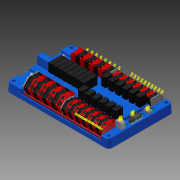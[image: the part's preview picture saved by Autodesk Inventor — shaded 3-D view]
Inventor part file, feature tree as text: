
AUTODESK INVENTOR PART (.ipt)
format: ipt  version: 2011 (Build 150239000, 239)  size: 17,145,856 bytes
history: native  units: in
note: dims shown in document units (in); Inventor stores cm internally (conversion verified against a paired STEP export)
features: other x181, sketch x22, plane x21, pattern_linear x3
ambient origin geometry x8: Origin, YZ Plane, XZ Plane, XY Plane, X Axis, Y Axis, Z Axis, Center Point
bodies: Solid1 (feature_tree)
feature tree (227):
  other  "PD Rev3 Assembly.iam"
  other  "PD Rev3 Bottom.ipt:1"
  other  "CTF040V8.iam:1::CTF040V8_1.ipt:1"
  other  "CTF040V8.iam:1::CTF040V8_2.ipt:1"
  other  "CTF040V8.iam:1::CTF040V8_3.ipt:1"
  other  "PD Rev3 PCB.iam:1::PD Rev3 Board.ipt:1"
  other  "PD Rev3 PCB.iam:1::Wago 745-831 (32A) Block.iam:1::Wago 745-831 (32A):1"
  other  "PD Rev3 PCB.iam:1::Wago 745-831 (32A) Block.iam:1::Wago 745-831 (32A):2"
  other  "PD Rev3 PCB.iam:1::Wago 745-831 (32A) Block.iam:1::Wago 745-831 (32A):3"
  other  "PD Rev3 PCB.iam:1::Wago 745-831 (32A) Block.iam:1::Wago 745-831 (32A):4"
  other  "PD Rev3 PCB.iam:1::Wago 745-831 (32A) Block.iam:1::Wago 745-831 (32A):5"
  other  "PD Rev3 PCB.iam:1::Wago 745-831 (32A) Block.iam:1::Wago 745-831 (32A):6"
  other  "PD Rev3 PCB.iam:1::Wago 745-831 (32A) Block.iam:1::Wago 745-831 (32A):7"
  other  "PD Rev3 PCB.iam:1::Wago 745-831 (32A) Block.iam:1::Wago 745-831 (32A):8"
  other  "PD Rev3 PCB.iam:1::Wago 745-831 (32A) Block.iam:1::Wago 745-831 (32A):9"
  other  "PD Rev3 PCB.iam:1::Wago 745-831 (32A) Block.iam:1::Wago 745-831 (32A):10"
  other  "PD Rev3 PCB.iam:1::Wago 745-831 (32A) Block.iam:1::Wago 745-831 (32A):11"
  other  "PD Rev3 PCB.iam:1::Wago 745-831 (32A) Block.iam:1::Wago 745-831 (32A):12"
  other  "PD Rev3 PCB.iam:1::Wago 745-831 (32A) Block.iam:1::745-300:1"
  other  "PD Rev3 PCB.iam:1::Wago 745-831 (32A) Block.iam:2::Wago 745-831 (32A):1"
  other  "PD Rev3 PCB.iam:1::Wago 745-831 (32A) Block.iam:2::Wago 745-831 (32A):2"
  other  "PD Rev3 PCB.iam:1::Wago 745-831 (32A) Block.iam:2::Wago 745-831 (32A):3"
  other  "PD Rev3 PCB.iam:1::Wago 745-831 (32A) Block.iam:2::Wago 745-831 (32A):4"
  other  "PD Rev3 PCB.iam:1::Wago 745-831 (32A) Block.iam:2::Wago 745-831 (32A):5"
  other  "PD Rev3 PCB.iam:1::Wago 745-831 (32A) Block.iam:2::Wago 745-831 (32A):6"
  other  "PD Rev3 PCB.iam:1::Wago 745-831 (32A) Block.iam:2::Wago 745-831 (32A):7"
  other  "PD Rev3 PCB.iam:1::Wago 745-831 (32A) Block.iam:2::Wago 745-831 (32A):8"
  other  "PD Rev3 PCB.iam:1::Wago 745-831 (32A) Block.iam:2::Wago 745-831 (32A):9"
  other  "PD Rev3 PCB.iam:1::Wago 745-831 (32A) Block.iam:2::Wago 745-831 (32A):10"
  other  "PD Rev3 PCB.iam:1::Wago 745-831 (32A) Block.iam:2::Wago 745-831 (32A):11"
  other  "PD Rev3 PCB.iam:1::Wago 745-831 (32A) Block.iam:2::Wago 745-831 (32A):12"
  other  "PD Rev3 PCB.iam:1::Wago 745-831 (32A) Block.iam:2::745-300:1"
  other  "PD Rev3 PCB.iam:1::Wago 745-851 (76A) Block.iam:1::Wago 745-851 (76A):2"
  other  "PD Rev3 PCB.iam:1::Wago 745-851 (76A) Block.iam:1::Wago 745-851 (76A):1"
  other  "PD Rev3 PCB.iam:1::Wago 745-851 (76A) Block.iam:1::Wago 745-851 (76A):3"
  other  "PD Rev3 PCB.iam:1::Wago 745-851 (76A) Block.iam:1::Wago 745-851 (76A):4"
  other  "PD Rev3 PCB.iam:1::Wago 745-851 (76A) Block.iam:1::Wago 745-851 (76A):5"
  other  "PD Rev3 PCB.iam:1::Wago 745-851 (76A) Block.iam:1::Wago 745-851 (76A):6"
  other  "PD Rev3 PCB.iam:1::Wago 745-851 (76A) Block.iam:1::Wago 745-851 (76A):7"
  other  "PD Rev3 PCB.iam:1::Wago 745-851 (76A) Block.iam:1::Wago 745-851 (76A):8"
  other  "PD Rev3 PCB.iam:1::Wago 745-851 (76A) Block.iam:1::745-500:1"
  other  "PD Rev3 PCB.iam:1::Wago 745-851 (76A) Block.iam:2::Wago 745-851 (76A):2"
  other  "PD Rev3 PCB.iam:1::Wago 745-851 (76A) Block.iam:2::Wago 745-851 (76A):1"
  other  "PD Rev3 PCB.iam:1::Wago 745-851 (76A) Block.iam:2::Wago 745-851 (76A):3"
  other  "PD Rev3 PCB.iam:1::Wago 745-851 (76A) Block.iam:2::Wago 745-851 (76A):4"
  other  "PD Rev3 PCB.iam:1::Wago 745-851 (76A) Block.iam:2::Wago 745-851 (76A):5"
  other  "PD Rev3 PCB.iam:1::Wago 745-851 (76A) Block.iam:2::Wago 745-851 (76A):6"
  other  "PD Rev3 PCB.iam:1::Wago 745-851 (76A) Block.iam:2::Wago 745-851 (76A):7"
  other  "PD Rev3 PCB.iam:1::Wago 745-851 (76A) Block.iam:2::Wago 745-851 (76A):8"
  other  "PD Rev3 PCB.iam:1::Wago 745-851 (76A) Block.iam:2::745-500:1"
  other  "PD Rev3 PCB.iam:1::LED.ipt:1"
  other  "PD Rev3 PCB.iam:1::LED.ipt:2"
  other  "PD Rev3 PCB.iam:1::734-132:1"
  other  "PD Rev3 PCB.iam:1::LED.ipt:3"
  other  "PD Rev3 PCB.iam:1::Wurth Lug.ipt:1"
  other  "PD Rev3 PCB.iam:1::Wurth Lug.ipt:2"
  other  "PD Rev3 PCB.iam:1::Big CB in Holder.ipt:1"
  other  "PD Rev3 PCB.iam:1::Big CB in Holder.ipt:2"
  other  "PD Rev3 PCB.iam:1::Big CB in Holder.ipt:3"
  other  "PD Rev3 PCB.iam:1::Big CB in Holder.ipt:4"
  other  "PD Rev3 PCB.iam:1::Big CB in Holder.ipt:5"
  other  "PD Rev3 PCB.iam:1::Big CB in Holder.ipt:6"
  other  "PD Rev3 PCB.iam:1::Big CB in Holder.ipt:7"
  other  "PD Rev3 PCB.iam:1::Big CB in Holder.ipt:8"
  other  "PD Rev3 PCB.iam:1::Medium CB in Holder.ipt:2"
  other  "PD Rev3 PCB.iam:1::Medium CB in Holder.ipt:1"
  other  "PD Rev3 PCB.iam:1::Medium CB in Holder.ipt:3"
  other  "PD Rev3 PCB.iam:1::Medium CB in Holder.ipt:4"
  other  "PD Rev3 PCB.iam:1::Medium CB in Holder.ipt:5"
  other  "PD Rev3 PCB.iam:1::Medium CB in Holder.ipt:6"
  other  "PD Rev3 PCB.iam:1::Medium CB in Holder.ipt:7"
  other  "PD Rev3 PCB.iam:1::Medium CB in Holder.ipt:8"
  other  "PD Rev3 PCB.iam:1::Medium CB in Holder.ipt:9"
  other  "PD Rev3 PCB.iam:1::Medium CB in Holder.ipt:10"
  other  "PD Rev3 PCB.iam:1::Medium CB in Holder.ipt:11"
  other  "PD Rev3 PCB.iam:1::Medium CB in Holder.ipt:12"
  other  "PD Rev3 PCB.iam:1::739-302:1"
  other  "PD Rev3 PCB.iam:1::CTM040V8.ipt:1"
  other  "PD Rev3 Top.ipt:1"
  other  "PD Rev3 Assembly.iam_Bodies"
  sketch  "Sketch2"  dims[d0=0.3937in]
  other  "Work Point2"
  other  "Work Point3"
  pattern_linear  "Rectangular Pattern1"  Count1=8 Spacing1=0.2953in
  sketch  "Sketch3"  dims[d1=0.125in]
  sketch  "Sketch4"  dims[d2=0.25in d3=3.1496in d5=0.2953in]
  sketch  "Sketch5"  dims[d6=0.125in]
  sketch  "Sketch6"  dims[d7=0.25in]
  sketch  "Sketch7"  dims[d8=0.125in]
  sketch  "Sketch8"  dims[d9=0.25in]
  sketch  "Sketch9"  dims[d10=0.125in]
  sketch  "Sketch10"  dims[d11=0.25in d12=3.1496in d14=0.2953in]
  sketch  "Sketch11"  dims[d15=0.125in]
  other  "Work Point27"
  other  "Work Point28"
  other  "Work Point29"
  other  "Work Point30"
  sketch  "Sketch12"  dims[d16=0.25in]
  sketch  "Sketch13"  dims[d17=0.125in]
  sketch  "Sketch14"  dims[d18=0.25in]
  sketch  "Sketch15"  dims[d19=0.125in]
  sketch  "Sketch16"  dims[d20=0.25in]
  sketch  "Sketch17"  dims[d21=0.125in]
  sketch  "Sketch18"  dims[d22=0.25in]
  sketch  "Sketch19"  dims[d23=0.125in]
  other  "Work Point39"
  other  "Work Point40"
  pattern_linear  "Rectangular Pattern2"  Count1=8 Spacing1=0.2953in
  other  "Work Point55"
  other  "Work Point56"
  other  "Work Point57"
  other  "Work Point58"
  other  "Work Point59"
  other  "Work Point60"
  sketch  "Sketch20"  dims[d24=0.25in]
  sketch  "Sketch21"  dims[d25=0.125in]
  other  "Work Point63"
  other  "Work Point64"
  other  "Work Point65"
  other  "Work Point66"
  sketch  "Sketch22"  dims[d26=0.25in]
  sketch  "Sketch23"  dims[d27=0.125in d28=3.1496in d30=0.3937in]
  other  "Work Point69"
  other  "Work Point70"
  other  "Work Point71"
  other  "Work Point72"
  other  "Work Point73"
  other  "Work Point74"
  other  "Work Point75"
  pattern_linear  "Rectangular Pattern3"  Count1=8 Spacing1=0.3937in
  plane  "Work Plane1"
  other  "Work Axis1"
  plane  "Work Plane2"
  other  "Work Axis2"
  other  "Work Point4"
  other  "Work Point5"
  other  "Work Point6"
  other  "Work Point7"
  other  "Work Point8"
  other  "Work Point9"
  other  "Work Point10"
  other  "Work Point11"
  other  "Work Point12"
  other  "Work Point13"
  other  "Work Point14"
  other  "Work Point15"
  other  "Work Point16"
  other  "Work Point17"
  plane  "Work Plane3"
  other  "Work Axis3"
  plane  "Work Plane4"
  other  "Work Axis4"
  plane  "Work Plane5"
  other  "Work Axis5"
  plane  "Work Plane6"
  other  "Work Axis6"
  plane  "Work Plane7"
  other  "Work Axis7"
  plane  "Work Plane8"
  other  "Work Axis8"
  other  "Work Point41"
  other  "Work Point42"
  other  "Work Point43"
  other  "Work Point44"
  other  "Work Point45"
  other  "Work Point46"
  other  "Work Point47"
  other  "Work Point48"
  other  "Work Point49"
  other  "Work Point50"
  other  "Work Point51"
  other  "Work Point52"
  other  "Work Point53"
  other  "Work Point54"
  other  "Work Axis9"
  other  "Work Axis10"
  other  "Work Axis11"
  other  "Work Axis12"
  plane  "Work Plane9"
  other  "Work Axis13"
  plane  "Work Plane10"
  other  "Work Axis14"
  plane  "Work Plane11"
  other  "Work Axis15"
  plane  "Work Plane12"
  other  "Work Axis16"
  plane  "Work Plane13"
  other  "Work Axis17"
  plane  "Work Plane14"
  other  "Work Axis18"
  plane  "Work Plane15"
  other  "Work Axis19"
  plane  "Work Plane16"
  other  "Work Axis20"
  plane  "Work Plane17"
  other  "Work Axis21"
  plane  "Work Plane18"
  other  "Work Axis22"
  plane  "Work Plane19"
  other  "Work Axis23"
  plane  "Work Plane20"
  other  "Work Axis24"
  other  "Work Axis25"
  other  "Work Axis26"
  plane  "Work Plane21"
  other  "Work Axis27"
  other  "Work Point76"
  other  "Work Point77"
  other  "Work Point78"
  other  "Work Point79"
  other  "Work Point80"
  other  "Work Point81"
  other  "Work Point82"
  other  "Work Point83"
  other  "Work Point84"
  other  "Work Point85"
  other  "Work Point86"
  other  "Work Point87"
  other  "Work Point88"
  other  "Work Point89"
  other  "Work Point90"
  other  "Work Point91"
  other  "Work Point92"
  other  "Work Point93"
  other  "Work Point94"
  other  "Work Point95"
  other  "Work Point96"
